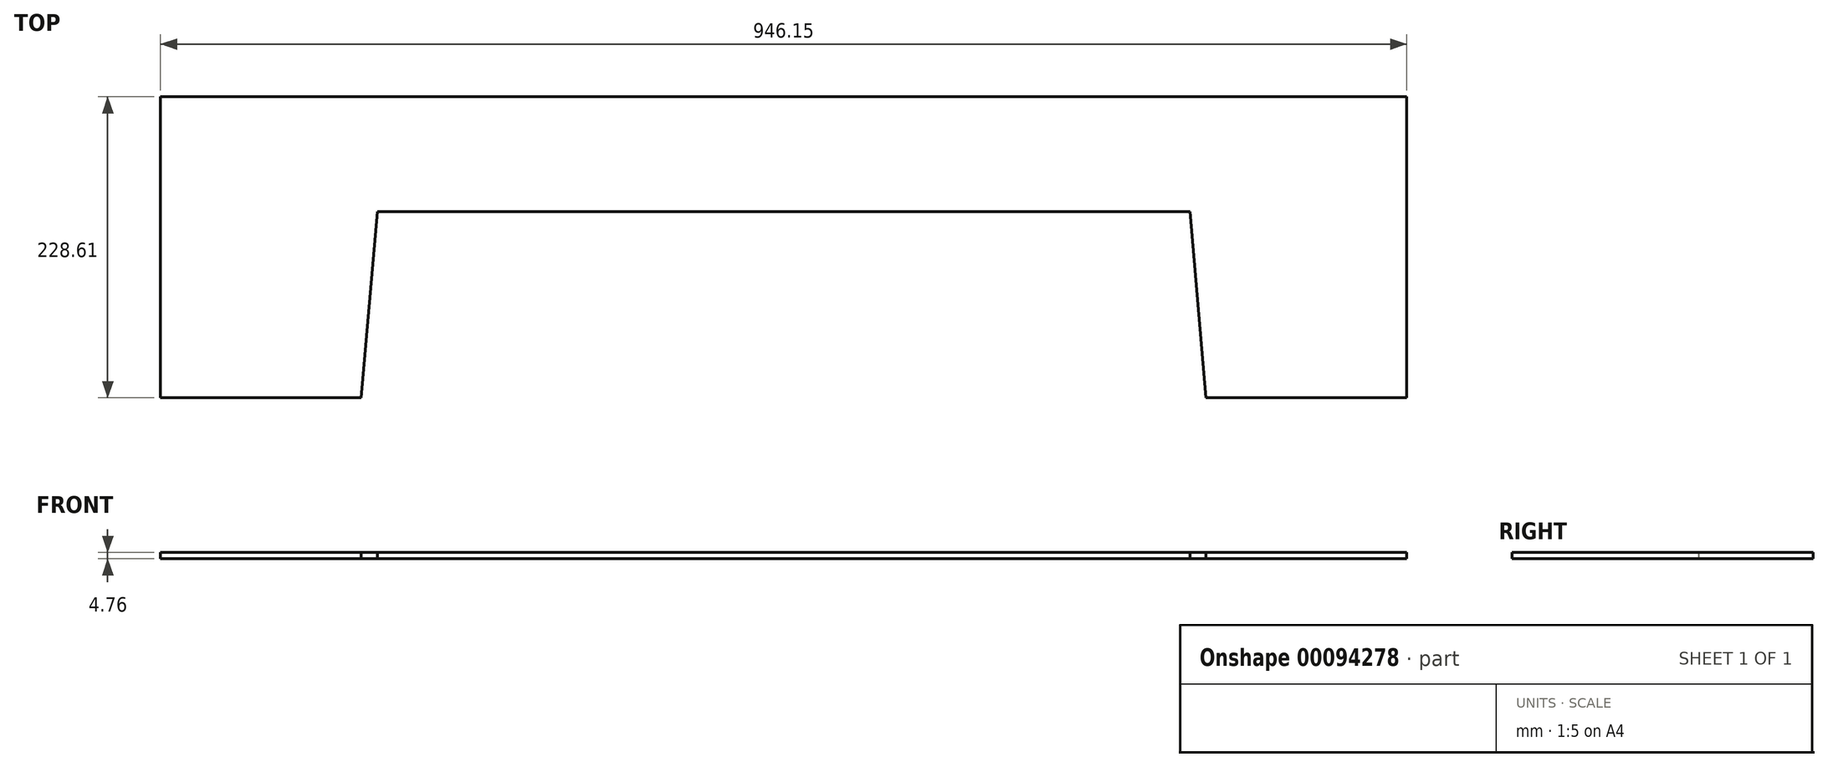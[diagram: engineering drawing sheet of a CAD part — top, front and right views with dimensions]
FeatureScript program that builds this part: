
annotation { "Feature Type Name" : "Feature", "Feature Type Description" : "" }
export const myFeature = defineFeature(function(context is Context, id is Id, definition is map)
    precondition{}
    {
        {
            var Q0;
            Q0=qCreatedBy(makeId("Top.planeOp"),FACE);
            var sketch = newSketch(context, id + "F0", { "sketchPlane" : qUnion([Q0])});
            skLineSegment(sketch, "E0.left", {"start": v(235.8, 115.25) * mm, "end": v(235.8, -113.35) * mm});
            skLineSegment(sketch, "E0.right", {"start": v(-710.36, 115.24) * mm, "end": v(-710.36, -113.36) * mm});
            skPoint(sketch, "E1.orphan", {"position": v(555.12, 48.59) * mm});
            skPoint(sketch, "E2.orphan", {"position": v(-557.96, -113.36) * mm});
            skLineSegment(sketch, "E3", {"start": v(-710.36, -113.36) * mm, "end": v(-557.96, -113.36) * mm});
            skLineSegment(sketch, "E4", {"start": v(83.4, -113.35) * mm, "end": v(235.8, -113.35) * mm});
            skLineSegment(sketch, "E5", {"start": v(-710.36, 115.24) * mm, "end": v(235.8, 115.25) * mm});
            skLineSegment(sketch, "E6.top", {"start": v(-545.73, 28.15) * mm, "end": v(71.15, 28.15) * mm});
            skLineSegment(sketch, "E7", {"start": v(-557.96, -113.36) * mm, "end": v(-545.73, 28.15) * mm});
            skLineSegment(sketch, "E8", {"start": v(83.4, -113.35) * mm, "end": v(71.15, 28.15) * mm});
            skSolve(sketch);
        }
        {
            var Q0;
            Q0 = qSketchRegion(id + "F0", true);
            extrude(context, id + "F1", {"entities" : qUnion([Q0]), "depth" : 4.76 * mm});
        }
    });
